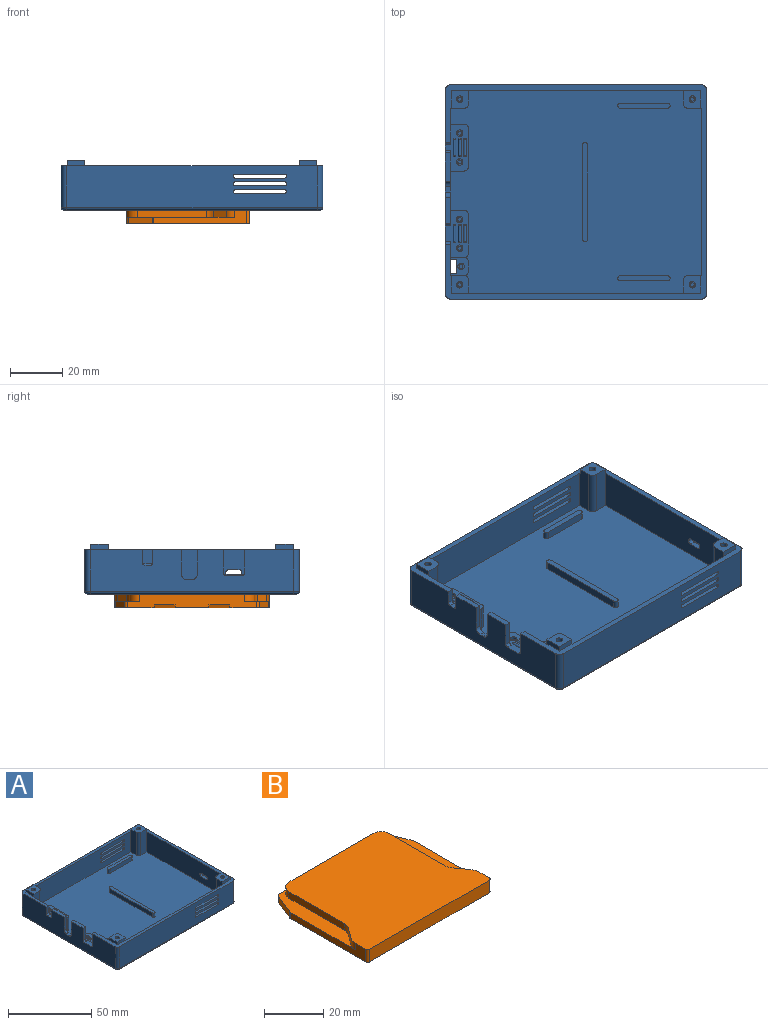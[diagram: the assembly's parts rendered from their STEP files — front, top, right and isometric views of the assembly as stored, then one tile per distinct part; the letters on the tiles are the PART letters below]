
ASSEMBLY  parts=2 mates=1
PART A: 208 faces, bbox 100.3x82.3x19 mm
  f0: plane 17x5mm, normal (1,0,0), area 84.5mm2, adj f13,f19,f23,f33,f34,f191
  f1: plane 17x5mm, normal (0,-1,0), area 84.5mm2, adj f16,f19,f23,f33,f34,f190
  f2: plane 17x5mm, normal (-1,0,0), area 84.5mm2, adj f13,f19,f23,f36,f37,f188
  f3: plane 17x5mm, normal (0,-1,0), area 84.5mm2, adj f19,f23,f24,f36,f37,f189
  f4: plane 6.75x6.75mm, normal (0,0,1), area 39.8mm2, adj f5,f6,f38,f160,f186,f187
  f5: plane 17x5mm, normal (-1,0,0), area 84.5mm2, adj f4,f11,f19,f23,f38,f186
  f6: plane 17x5mm, normal (0,1,0), area 84.5mm2, adj f4,f19,f23,f24,f38,f187
  f7: plane 6.75x6.75mm, normal (0,0,1), area 39.8mm2, adj f8,f9,f35,f156,f184,f185
  f8: plane 17x5mm, normal (1,0,0), area 84.5mm2, adj f7,f11,f19,f23,f35,f184
  f9: plane 7x5mm, normal (0,1,0), area 34.5mm2, adj f7,f18,f19,f35,f173,f185
  f10: plane 98x80mm, normal (0,0,-1), area 7826.7mm2, adj f18,f145,f146,f147,f148,f149,f150,f151
  f11: plane 82x15mm, normal (0,1,0), area 1140.6mm2, adj f5,f8,f19,f23,f121,f122,f123,f124
  f12: plane 96x16mm, normal (0,-1,0), area 1446.6mm2, adj f19,f26,f27,f121,f122,f123,f124,f125
  f13: plane 82x15mm, normal (0,-1,0), area 1140.6mm2, adj f0,f2,f19,f23,f97,f98,f99,f100
  f14: plane 96x16mm, normal (0,1,0), area 1446.6mm2, adj f19,f25,f29,f97,f98,f99,f100,f101
  f15: plane 18x9mm, normal (0,0,1), area 97.5mm2, adj f16,f21,f22,f64,f65,f83,f84,f85
  f16: plane 15x14mm, normal (1,0,0), area 132.2mm2, adj f1,f15,f19,f23,f63,f64,f83
  f17: plane 18x9mm, normal (0,0,1), area 105.5mm2, adj f18,f21,f22,f68,f69,f70,f71,f72
  f18: plane 17x13mm, normal (1,0,0), area 150mm2, adj f9,f10,f17,f19,f67,f69,f169,f173
  f19: plane 100x82mm, normal (0,0,1), area 644.3mm2, adj f0,f1,f2,f3,f5,f6,f8,f9
  f20: plane 11x2mm, normal (0,0,1), area 22mm2, adj f21,f22,f30,f62
  f21: plane 29x15mm, normal (1,0,0), area 250.2mm2, adj f15,f17,f20,f23,f30,f31,f32,f62
  f22: plane 78x16mm, normal (-1,0,0), area 1077.6mm2, adj f15,f17,f19,f20,f25,f26,f30,f31
  f23: plane 96x78mm, normal (0,0,1), area 6846.2mm2, adj f0,f1,f2,f3,f5,f6,f8,f11
  f24: plane 64x15mm, normal (-1,0,0), area 945.9mm2, adj f3,f6,f19,f23,f54,f55,f56,f57
  f25: cylinder r=2mm len=16mm, axis (0,0,-1), area 50.3mm2, adj f14,f19,f22,f151
  f26: cylinder r=2mm len=16mm, axis (0,0,-1), area 50.3mm2, adj f12,f19,f22,f150
  f27: cylinder r=2mm len=16mm, axis (0,0,-1), area 50.3mm2, adj f12,f19,f28,f146
  f28: plane 78x16mm, normal (1,0,0), area 1233.9mm2, adj f19,f27,f29,f54,f55,f56,f57,f58
  f29: cylinder r=2mm len=16mm, axis (0,0,-1), area 50.3mm2, adj f14,f19,f28,f147
  f30: plane 9.49x2mm, normal (0,-1,0), area 19mm2, adj f20,f21,f22,f182
  f31: plane 9.49x2mm, normal (0,1,0), area 19mm2, adj f21,f22,f32,f183
  f32: plane 10x2mm, normal (0,0,1), area 20mm2, adj f21,f22,f31,f66
  f33: cylinder r=2mm len=17mm, axis (0,0,-1), area 53.4mm2, adj f0,f1,f23,f34
  f34: plane 6.75x6.75mm, normal (0,0,1), area 39.8mm2, adj f0,f1,f33,f154,f190,f191
  f35: cylinder r=2mm len=17mm, axis (0,0,-1), area 53.4mm2, adj f7,f8,f9,f23,f170
  f36: cylinder r=2mm len=17mm, axis (0,0,-1), area 53.4mm2, adj f2,f3,f23,f37
  f37: plane 6.75x6.75mm, normal (0,0,1), area 39.8mm2, adj f2,f3,f36,f158,f188,f189
  f38: cylinder r=2mm len=17mm, axis (0,0,-1), area 53.4mm2, adj f4,f5,f6,f23
  f39: cylinder r=1mm len=3mm, axis (0,0,-1), area 9.4mm2, adj f23,f40,f42,f43
  f40: plane 36x3mm, normal (1,0,0), area 108mm2, adj f23,f39,f41,f43
  f41: cylinder r=1mm len=3mm, axis (0,0,-1), area 9.4mm2, adj f23,f40,f42,f43
  f42: plane 36x3mm, normal (-1,0,0), area 108mm2, adj f23,f39,f41,f43
  f43: plane 38x2mm, normal (0,0,1), area 75.1mm2, adj f39,f40,f41,f42
  f44: cylinder r=1mm len=3mm, axis (0,0,-1), area 9.4mm2, adj f23,f45,f47,f48
  f45: plane 18x3mm, normal (0,-1,0), area 54mm2, adj f23,f44,f46,f48
  f46: cylinder r=1mm len=3mm, axis (0,0,-1), area 9.4mm2, adj f23,f45,f47,f48
  f47: plane 18x3mm, normal (0,1,0), area 54mm2, adj f23,f44,f46,f48
  f48: plane 20x2mm, normal (0,0,1), area 39.1mm2, adj f44,f45,f46,f47
  f49: cylinder r=1mm len=3mm, axis (0,0,-1), area 9.4mm2, adj f23,f50,f52,f53
  f50: plane 18x3mm, normal (0,-1,0), area 54mm2, adj f23,f49,f51,f53
  f51: cylinder r=1mm len=3mm, axis (0,0,-1), area 9.4mm2, adj f23,f50,f52,f53
  f52: plane 18x3mm, normal (0,1,0), area 54mm2, adj f23,f49,f51,f53
  f53: plane 20x2mm, normal (0,0,1), area 39.1mm2, adj f49,f50,f51,f52
  f54: cylinder r=1mm len=2mm, axis (1,0,0), area 3.1mm2, adj f24,f28,f55,f61
  f55: plane 4x2mm, normal (0,0,1), area 8mm2, adj f24,f28,f54,f56
  f56: cylinder r=1mm len=2mm, axis (1,0,0), area 3.1mm2, adj f24,f28,f55,f57
  f57: plane 2x0.5mm, normal (0,-1,0), area 1mm2, adj f24,f28,f56,f58
  f58: cylinder r=1mm len=2mm, axis (1,0,0), area 3.1mm2, adj f24,f28,f57,f59
  f59: plane 4x2mm, normal (0,0,-1), area 8mm2, adj f24,f28,f58,f60
  f60: cylinder r=1mm len=2mm, axis (1,0,0), area 3.1mm2, adj f24,f28,f59,f61
  f61: plane 2x0.5mm, normal (0,1,0), area 1mm2, adj f24,f28,f54,f60
  f62: plane 5x2mm, normal (0,1,0), area 10mm2, adj f20,f21,f22,f65
  f63: plane 5x2mm, normal (0,-1,0), area 10mm2, adj f16,f19,f22,f64
  f64: cylinder r=1mm len=2mm, axis (1,0,0), area 3.1mm2, adj f15,f16,f22,f63
  f65: cylinder r=1mm len=2mm, axis (-1,0,0), area 3.1mm2, adj f15,f21,f22,f62
  f66: plane 9x2mm, normal (0,-1,0), area 18mm2, adj f21,f22,f32,f68
  f67: plane 9x2mm, normal (0,1,0), area 18mm2, adj f18,f19,f22,f69
  f68: cylinder r=1mm len=2mm, axis (-1,0,0), area 3.1mm2, adj f17,f21,f22,f66
  f69: cylinder r=1mm len=2mm, axis (1,0,0), area 3.1mm2, adj f17,f18,f22,f67
  f70: plane 5x5mm, normal (0,1,0), area 25mm2, adj f17,f21,f23,f72
  f71: plane 14x5mm, normal (1,0,0), area 70mm2, adj f17,f23,f72,f73
  f72: cylinder r=2mm len=5mm, axis (0,0,-1), area 15.7mm2, adj f17,f23,f70,f71
  f73: cylinder r=2mm len=5mm, axis (0,0,1), area 15.7mm2, adj f17,f23,f71,f172
  f74: cylinder r=0.5mm len=1mm, axis (1,0,0), area 0.5mm2, adj f17,f75
  f75: cylinder r=0.5mm len=7mm, axis (0,1,0), area 10.4mm2, adj f17,f74,f76
  f76: cylinder r=0.5mm len=1mm, axis (-1,0,0), area 0.5mm2, adj f17,f75
  f77: cylinder r=0.5mm len=7mm, axis (0,1,0), area 10.4mm2, adj f17,f78,f79
  f78: cylinder r=0.5mm len=1mm, axis (1,0,0), area 0.5mm2, adj f17,f77
  f79: cylinder r=0.5mm len=1mm, axis (-1,0,0), area 0.5mm2, adj f17,f77
  f80: cylinder r=0.5mm len=1mm, axis (1,0,0), area 0.5mm2, adj f17,f81
  f81: cylinder r=0.5mm len=7mm, axis (0,1,0), area 10.4mm2, adj f17,f80,f82
  f82: cylinder r=0.5mm len=1mm, axis (-1,0,0), area 0.5mm2, adj f17,f81
  f83: plane 9x5mm, normal (0,1,0), area 45mm2, adj f15,f16,f23,f86
  f84: plane 9x5mm, normal (0,-1,0), area 45mm2, adj f15,f21,f23,f87
  f85: plane 14x9mm, normal (1,0,0), area 126mm2, adj f15,f23,f86,f87
  f86: cylinder r=2mm len=9mm, axis (0,0,-1), area 28.3mm2, adj f15,f23,f83,f85
  f87: cylinder r=2mm len=9mm, axis (0,0,1), area 28.3mm2, adj f15,f23,f84,f85
  f88: cylinder r=0.5mm len=1mm, axis (1,0,0), area 0.5mm2, adj f15,f89
  f89: cylinder r=0.5mm len=7mm, axis (0,1,0), area 10.4mm2, adj f15,f88,f90
  f90: cylinder r=0.5mm len=1mm, axis (-1,0,0), area 0.5mm2, adj f15,f89
  f91: cylinder r=0.5mm len=7mm, axis (0,1,0), area 10.4mm2, adj f15,f92,f93
  f92: cylinder r=0.5mm len=1mm, axis (1,0,0), area 0.5mm2, adj f15,f91
  f93: cylinder r=0.5mm len=1mm, axis (-1,0,0), area 0.5mm2, adj f15,f91
  f94: cylinder r=0.5mm len=1mm, axis (1,0,0), area 0.5mm2, adj f15,f95
  f95: cylinder r=0.5mm len=7mm, axis (0,1,0), area 10.4mm2, adj f15,f94,f96
  f96: cylinder r=0.5mm len=1mm, axis (-1,0,0), area 0.5mm2, adj f15,f95
  f97: plane 2x0.5mm, normal (1,0,0), area 1mm2, adj f13,f14,f109,f112
  f98: plane 19x2mm, normal (0,0,1), area 38mm2, adj f13,f14,f111,f112
  f99: plane 2x0.5mm, normal (-1,0,0), area 1mm2, adj f13,f14,f110,f111
  f100: plane 19x2mm, normal (0,0,-1), area 38mm2, adj f13,f14,f109,f110
  f101: plane 2x0.5mm, normal (1,0,0), area 1mm2, adj f13,f14,f113,f116
  f102: plane 19x2mm, normal (0,0,1), area 38mm2, adj f13,f14,f113,f114
  f103: plane 2x0.5mm, normal (-1,0,0), area 1mm2, adj f13,f14,f114,f115
  f104: plane 19x2mm, normal (0,0,-1), area 38mm2, adj f13,f14,f115,f116
  f105: plane 19x2mm, normal (0,0,1), area 38mm2, adj f13,f14,f117,f120
  f106: plane 2x0.5mm, normal (-1,0,0), area 1mm2, adj f13,f14,f119,f120
  f107: plane 19x2mm, normal (0,0,-1), area 38mm2, adj f13,f14,f118,f119
  f108: plane 2x0.5mm, normal (1,0,0), area 1mm2, adj f13,f14,f117,f118
  f109: cylinder r=0.5mm len=2mm, axis (0,-1,0), area 1.6mm2, adj f13,f14,f97,f100
  f110: cylinder r=0.5mm len=2mm, axis (0,1,0), area 1.6mm2, adj f13,f14,f99,f100
  f111: cylinder r=0.5mm len=2mm, axis (0,-1,0), area 1.6mm2, adj f13,f14,f98,f99
  f112: cylinder r=0.5mm len=2mm, axis (0,1,0), area 1.6mm2, adj f13,f14,f97,f98
  f113: cylinder r=0.5mm len=2mm, axis (0,1,0), area 1.6mm2, adj f13,f14,f101,f102
  f114: cylinder r=0.5mm len=2mm, axis (0,-1,0), area 1.6mm2, adj f13,f14,f102,f103
  f115: cylinder r=0.5mm len=2mm, axis (0,1,0), area 1.6mm2, adj f13,f14,f103,f104
  f116: cylinder r=0.5mm len=2mm, axis (0,-1,0), area 1.6mm2, adj f13,f14,f101,f104
  f117: cylinder r=0.5mm len=2mm, axis (0,-1,0), area 1.6mm2, adj f13,f14,f105,f108
  f118: cylinder r=0.5mm len=2mm, axis (0,1,0), area 1.6mm2, adj f13,f14,f107,f108
  f119: cylinder r=0.5mm len=2mm, axis (0,-1,0), area 1.6mm2, adj f13,f14,f106,f107
  f120: cylinder r=0.5mm len=2mm, axis (0,1,0), area 1.6mm2, adj f13,f14,f105,f106
  f121: plane 2x0.5mm, normal (-1,0,0), area 1mm2, adj f11,f12,f133,f136
  f122: plane 19x2mm, normal (0,0,1), area 38mm2, adj f11,f12,f135,f136
  f123: plane 2x0.5mm, normal (1,0,0), area 1mm2, adj f11,f12,f134,f135
  f124: plane 19x2mm, normal (0,0,-1), area 38mm2, adj f11,f12,f133,f134
  f125: plane 2x0.5mm, normal (-1,0,0), area 1mm2, adj f11,f12,f137,f140
  f126: plane 19x2mm, normal (0,0,1), area 38mm2, adj f11,f12,f137,f138
  f127: plane 2x0.5mm, normal (1,0,0), area 1mm2, adj f11,f12,f138,f139
  f128: plane 19x2mm, normal (0,0,-1), area 38mm2, adj f11,f12,f139,f140
  f129: plane 19x2mm, normal (0,0,1), area 38mm2, adj f11,f12,f141,f144
  f130: plane 2x0.5mm, normal (1,0,0), area 1mm2, adj f11,f12,f143,f144
  f131: plane 19x2mm, normal (0,0,-1), area 38mm2, adj f11,f12,f142,f143
  f132: plane 2x0.5mm, normal (-1,0,0), area 1mm2, adj f11,f12,f141,f142
  f133: cylinder r=0.5mm len=2mm, axis (0,1,0), area 1.6mm2, adj f11,f12,f121,f124
  f134: cylinder r=0.5mm len=2mm, axis (0,-1,0), area 1.6mm2, adj f11,f12,f123,f124
  f135: cylinder r=0.5mm len=2mm, axis (0,1,0), area 1.6mm2, adj f11,f12,f122,f123
  f136: cylinder r=0.5mm len=2mm, axis (0,-1,0), area 1.6mm2, adj f11,f12,f121,f122
  f137: cylinder r=0.5mm len=2mm, axis (0,-1,0), area 1.6mm2, adj f11,f12,f125,f126
  f138: cylinder r=0.5mm len=2mm, axis (0,1,0), area 1.6mm2, adj f11,f12,f126,f127
  f139: cylinder r=0.5mm len=2mm, axis (0,-1,0), area 1.6mm2, adj f11,f12,f127,f128
  f140: cylinder r=0.5mm len=2mm, axis (0,1,0), area 1.6mm2, adj f11,f12,f125,f128
  f141: cylinder r=0.5mm len=2mm, axis (0,1,0), area 1.6mm2, adj f11,f12,f129,f132
  f142: cylinder r=0.5mm len=2mm, axis (0,-1,0), area 1.6mm2, adj f11,f12,f131,f132
  f143: cylinder r=0.5mm len=2mm, axis (0,1,0), area 1.6mm2, adj f11,f12,f130,f131
  f144: cylinder r=0.5mm len=2mm, axis (0,-1,0), area 1.6mm2, adj f11,f12,f129,f130
  f145: cylinder r=1mm len=78mm, axis (0,1,0), area 122.5mm2, adj f10,f28,f146,f147
  f146: torus R=1mm, axis (0,0,1), area 4mm2, adj f10,f27,f145,f148
  f147: torus R=1mm, axis (0,0,1), area 4mm2, adj f10,f29,f145,f149
  f148: cylinder r=1mm len=96mm, axis (1,0,0), area 150.8mm2, adj f10,f12,f146,f150
  f149: cylinder r=1mm len=96mm, axis (-1,0,0), area 150.8mm2, adj f10,f14,f147,f151
  f150: torus R=1mm, axis (0,0,1), area 4mm2, adj f10,f26,f148,f152
  f151: torus R=1mm, axis (0,0,1), area 4mm2, adj f10,f25,f149,f152
  f152: cylinder r=1mm len=78mm, axis (0,-1,0), area 122.5mm2, adj f10,f22,f150,f151
  f153: plane 2.5x2.5mm, normal (0,0,1), area 3.1mm2, adj f154,f162
  f154: cylinder r=1.25mm len=5mm, axis (0,0,1), area 39.3mm2, adj f34,f153
  f155: plane 2.5x2.5mm, normal (0,0,1), area 3.1mm2, adj f156,f164
  f156: cylinder r=1.25mm len=5mm, axis (0,0,1), area 39.3mm2, adj f7,f155
  f157: plane 2.5x2.5mm, normal (0,0,1), area 3.1mm2, adj f158,f166
  f158: cylinder r=1.25mm len=5mm, axis (0,0,1), area 39.3mm2, adj f37,f157
  f159: plane 2.5x2.5mm, normal (0,0,1), area 3.1mm2, adj f160,f168
  f160: cylinder r=1.25mm len=5mm, axis (0,0,1), area 39.3mm2, adj f4,f159
  f161: plane 1.5x1.5mm, normal (0,0,1), area 1.8mm2, adj f162
  f162: cylinder r=0.75mm len=12mm, axis (0,0,1), area 56.5mm2, adj f153,f161
  f163: plane 1.5x1.5mm, normal (0,0,1), area 1.8mm2, adj f164
  f164: cylinder r=0.75mm len=12mm, axis (0,0,1), area 56.5mm2, adj f155,f163
  f165: plane 1.5x1.5mm, normal (0,0,1), area 1.8mm2, adj f166
  f166: cylinder r=0.75mm len=12mm, axis (0,0,1), area 56.5mm2, adj f157,f165
  f167: plane 1.5x1.5mm, normal (0,0,1), area 1.8mm2, adj f168
  f168: cylinder r=0.75mm len=12mm, axis (0,0,1), area 56.5mm2, adj f159,f167
  f169: plane 5x5mm, normal (0,1,0), area 25mm2, adj f17,f18,f172,f173
  f170: cylinder r=2mm len=10mm, axis (0,0,-1), area 31.4mm2, adj f23,f35,f171,f173
  f171: plane 10x3mm, normal (1,0,0), area 30mm2, adj f23,f170,f172,f173
  f172: cylinder r=2mm len=10mm, axis (0,0,-1), area 31.4mm2, adj f23,f73,f169,f171,f173
  f173: plane 7x7mm, normal (0,0,1), area 30mm2, adj f9,f18,f169,f170,f171,f172,f174,f175
  f174: plane 12x2.3mm, normal (0,1,0), area 27.6mm2, adj f10,f18,f173,f175
  f175: plane 12x5.4mm, normal (-1,0,0), area 64.8mm2, adj f10,f173,f174,f176
  f176: plane 12x2.3mm, normal (0,-1,0), area 27.6mm2, adj f10,f18,f173,f175
  f177: cylinder r=1.25mm len=5mm, axis (0,0,1), area 39.3mm2, adj f173,f178
  f178: plane 2.5x2.5mm, normal (0,0,1), area 3.1mm2, adj f177,f179
  f179: cylinder r=0.75mm len=5mm, axis (0,0,1), area 23.6mm2, adj f178,f180
  f180: plane 1.5x1.5mm, normal (0,0,1), area 1.8mm2, adj f179
  f181: plane 2x2mm, normal (0,0,1), area 4mm2, adj f21,f22,f182,f183
  f182: cylinder r=2mm len=2mm, axis (-1,0,0), area 6.3mm2, adj f21,f22,f30,f181
  f183: cylinder r=2mm len=2mm, axis (1,0,0), area 6.3mm2, adj f21,f22,f31,f181
  f184: plane 6.75x2mm, normal (0,-1,0), area 13.5mm2, adj f7,f8,f19,f185
  f185: plane 6.75x2mm, normal (-1,0,0), area 13.5mm2, adj f7,f9,f19,f184
  f186: plane 6.75x2mm, normal (0,-1,0), area 13.5mm2, adj f4,f5,f19,f187
  f187: plane 6.75x2mm, normal (1,0,0), area 13.5mm2, adj f4,f6,f19,f186
  f188: plane 6.75x2mm, normal (0,1,0), area 13.5mm2, adj f2,f19,f37,f189
  f189: plane 6.75x2mm, normal (1,0,0), area 13.5mm2, adj f3,f19,f37,f188
  f190: plane 6.75x2mm, normal (-1,0,0), area 13.5mm2, adj f1,f19,f34,f191
  f191: plane 6.75x2mm, normal (0,1,0), area 13.5mm2, adj f0,f19,f34,f190
  f192: plane 2.5x2.5mm, normal (0,0,1), area 3.1mm2, adj f193,f197
  f193: cylinder r=1.25mm len=2.5mm, axis (0,0,1), area 7.9mm2, adj f15,f192
  f194: plane 2.5x2.5mm, normal (0,0,1), area 3.1mm2, adj f195,f199
  f195: cylinder r=1.25mm len=2.5mm, axis (0,0,1), area 7.9mm2, adj f15,f194
  f196: plane 1.5x1.5mm, normal (0,0,1), area 1.8mm2, adj f197
  f197: cylinder r=0.75mm len=6mm, axis (0,0,1), area 28.3mm2, adj f192,f196
  f198: plane 1.5x1.5mm, normal (0,0,1), area 1.8mm2, adj f199
  f199: cylinder r=0.75mm len=6mm, axis (0,0,1), area 28.3mm2, adj f194,f198
  f200: plane 2.5x2.5mm, normal (0,0,1), area 3.1mm2, adj f201,f205
  f201: cylinder r=1.25mm len=2.5mm, axis (0,0,1), area 7.9mm2, adj f17,f200
  f202: plane 2.5x2.5mm, normal (0,0,1), area 3.1mm2, adj f203,f207
  f203: cylinder r=1.25mm len=2.5mm, axis (0,0,1), area 7.9mm2, adj f17,f202
  f204: plane 1.5x1.5mm, normal (0,0,1), area 1.8mm2, adj f205
  f205: cylinder r=0.75mm len=4mm, axis (0,0,1), area 18.8mm2, adj f200,f204
  f206: plane 1.5x1.5mm, normal (0,0,1), area 1.8mm2, adj f207
  f207: cylinder r=0.75mm len=4mm, axis (0,0,1), area 18.8mm2, adj f202,f206
PART B: 36 faces, bbox 59x47x5.2 mm
  f0: plane 49.65x5.2mm, normal (0,1,0), area 214.5mm2, adj f1,f2,f8,f11,f12,f15,f19,f20
  f1: plane 59x47mm, normal (0,0,-1), area 2467.3mm2, adj f0,f3,f4,f5,f6,f7,f16,f17
  f2: plane 41.14x9.5mm, normal (0,0,1), area 180mm2, adj f0,f5,f6,f9,f10,f11,f18,f19
  f3: plane 35.81x5.2mm, normal (-1,0,0), area 102.6mm2, adj f1,f8,f15,f16,f21,f24
  f4: plane 57x5.2mm, normal (0,-1,0), area 296.4mm2, adj f1,f15,f16,f17
  f5: plane 35.81x5.2mm, normal (1,0,0), area 102.6mm2, adj f1,f2,f15,f17,f18,f25
  f6: plane 9.19x3.68mm, normal (0.93,0.37,0), area 24.8mm2, adj f1,f2,f18,f19
  f7: plane 9.19x3.68mm, normal (-0.93,0.37,0), area 24.8mm2, adj f1,f8,f20,f21
  f8: plane 41.14x9.5mm, normal (0,0,1), area 180mm2, adj f0,f3,f7,f12,f13,f14,f20,f21
  f9: plane 4.86x3.56mm, normal (0.81,0.59,0), area 16.3mm2, adj f2,f15,f22,f25
  f10: plane 26.36x2.7mm, normal (1,0,0), area 71.2mm2, adj f2,f11,f15,f22
  f11: cylinder r=4mm len=4mm, axis (0,0,-1), area 17mm2, adj f0,f2,f10,f15
  f12: cylinder r=4mm len=4mm, axis (0,0,-1), area 17mm2, adj f0,f8,f13,f15
  f13: plane 26.36x2.7mm, normal (-1,0,0), area 71.2mm2, adj f8,f12,f15,f23
  f14: plane 4.86x3.56mm, normal (-0.81,0.59,0), area 16.3mm2, adj f8,f15,f23,f24
  f15: plane 59x47mm, normal (0,0,1), area 2372.5mm2, adj f0,f3,f4,f5,f9,f10,f11,f12
  f16: cylinder r=1mm len=5.2mm, axis (0,0,-1), area 8.2mm2, adj f1,f3,f4,f15
  f17: cylinder r=1mm len=5.2mm, axis (0,0,1), area 8.2mm2, adj f1,f4,f5,f15
  f18: cylinder r=1mm len=2.5mm, axis (0,0,-1), area 1mm2, adj f1,f2,f5,f6
  f19: cylinder r=1mm len=2.5mm, axis (0,0,-1), area 3mm2, adj f0,f1,f2,f6
  f20: cylinder r=1mm len=2.5mm, axis (0,0,1), area 3mm2, adj f0,f1,f7,f8
  f21: cylinder r=1mm len=2.5mm, axis (0,0,-1), area 1mm2, adj f1,f3,f7,f8
  f22: cylinder r=5mm len=2.96mm, axis (0,0,-1), area 8.5mm2, adj f2,f9,f10,f15
  f23: cylinder r=5mm len=2.96mm, axis (0,0,-1), area 8.5mm2, adj f8,f13,f14,f15
  f24: cylinder r=5mm len=2.96mm, axis (0,0,-1), area 8.5mm2, adj f3,f8,f14,f15
  f25: cylinder r=5mm len=2.96mm, axis (0,0,-1), area 8.5mm2, adj f2,f5,f9,f15
  f26: plane 0.54x0.54mm, normal (0,0,-1), area 0.2mm2, adj f34
  f27: plane 0.54x0.54mm, normal (0,0,-1), area 0.2mm2, adj f35
  f28: plane 15x1.1mm, normal (-1,0,0), area 8.3mm2, adj f0,f1,f32
  f29: plane 15x1.1mm, normal (1,0,0), area 8.2mm2, adj f0,f1,f32
  f30: plane 15x1.1mm, normal (1,0,0), area 8.2mm2, adj f0,f1,f33
  f31: plane 15x1.1mm, normal (-1,0,0), area 8.2mm2, adj f0,f1,f33
  f32: plane 15x8mm, normal (0,0.07,-1), area 120.3mm2, adj f0,f1,f28,f29
  f33: plane 15x8mm, normal (0,0.07,-1), area 120.3mm2, adj f0,f1,f30,f31
  f34: torus R=0.27mm, axis (0,0,1), area 16.1mm2, adj f1,f26
  f35: torus R=0.27mm, axis (0,0,1), area 16.1mm2, adj f1,f27
PLACE A t=(11.75,4.23,9.55)mm
PLACE B rot(axis=(0,0,1),90deg) t=(36.75,15.73,4.35)mm
MATE fastened B.f15 <-> A.f10  axis (0,0,1) through (36.75,45.23,9.55)mm
